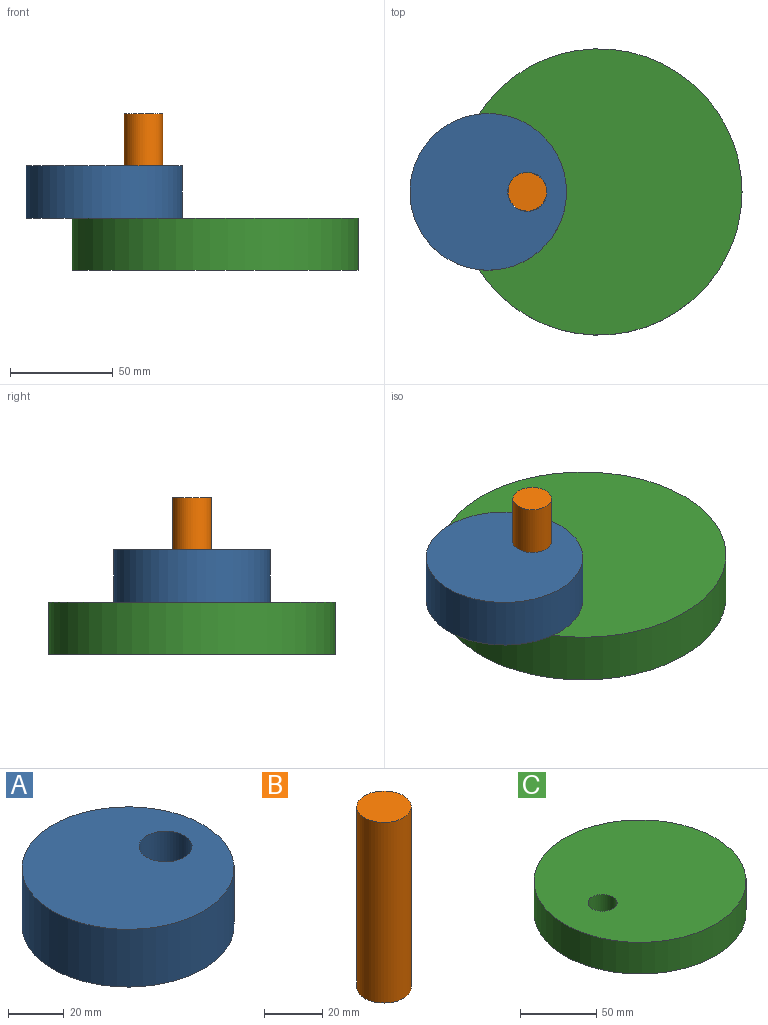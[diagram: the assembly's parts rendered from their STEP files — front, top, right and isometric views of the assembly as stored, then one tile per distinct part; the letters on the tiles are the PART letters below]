
ASSEMBLY  parts=3 mates=3
PART A: 4 faces, bbox 76.2x76.2x25.4 mm
  f0: cylinder r=38.1mm len=76.2mm, axis (0,0,-1), area 6080.5mm2, adj f1,f2
  f1: plane 76.2x76.2mm, normal (0,0,1), area 4275.3mm2, adj f0,f3
  f2: plane 76.2x76.2mm, normal (0,0,-1), area 4275.3mm2, adj f0,f3
  f3: cylinder r=9.53mm len=25.4mm, axis (0,0,1), area 1520.1mm2, adj f1,f2
PART B: 3 faces, bbox 18.8x18.8x76.2 mm
  f0: cylinder r=9.4mm len=76.2mm, axis (0,0,-1), area 4499.6mm2, adj f1,f2
  f1: plane 18.8x18.8mm, normal (0,0,1), area 277.5mm2, adj f0
  f2: plane 18.8x18.8mm, normal (0,0,-1), area 277.5mm2, adj f0
PART C: 4 faces, bbox 139.3x139.3x25.4 mm
  f0: cylinder r=69.64mm len=139.28mm, axis (0,0,-1), area 11113.8mm2, adj f1,f2
  f1: plane 139.28x139.28mm, normal (0,0,1), area 14950.2mm2, adj f0,f3
  f2: plane 139.28x139.28mm, normal (0,0,-1), area 14950.2mm2, adj f0,f3
  f3: cylinder r=9.53mm len=25.4mm, axis (0,0,1), area 1520.1mm2, adj f1,f2
PLACE A t=(-19.05,0,-12.7)mm
PLACE B rot(axis=(1,0,0),180deg) t=(69.69,-47.98,38.1)mm
PLACE C t=(91.06,38.16,-38.1)mm
MATE revolute A.f3 <-> B.f0  axis (0,0,1) through (0,0,0)mm
MATE revolute C.f3 <-> B.f0  axis (0,0,-1) through (0,0,-38.1)mm
MATE slider A.f3 <-> C.f3  axis (0,0,-1) through (0,0,-12.7)mm
